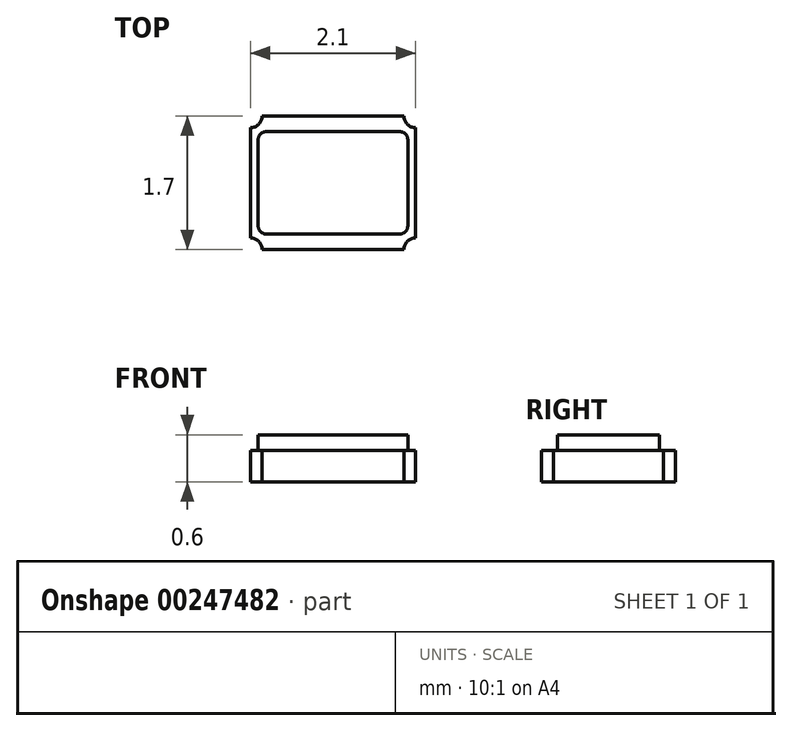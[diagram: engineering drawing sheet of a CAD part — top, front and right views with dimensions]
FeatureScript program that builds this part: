
annotation { "Feature Type Name" : "Feature", "Feature Type Description" : "" }
export const myFeature = defineFeature(function(context is Context, id is Id, definition is map)
    precondition{}
    {
        {
            var Q0;
            Q0=qCreatedBy(makeId("Top.planeOp"),FACE);
            var sketch = newSketch(context, id + "F0", { "sketchPlane" : qUnion([Q0])});
            skLineSegment(sketch, "E0.bottom", {"start": v(0.9, -0.85) * mm, "end": v(-0.9, -0.85) * mm});
            skLineSegment(sketch, "E0.top", {"start": v(0.9, 0.85) * mm, "end": v(-0.9, 0.85) * mm});
            skLineSegment(sketch, "E0.left", {"start": v(1.05, -0.7) * mm, "end": v(1.05, 0.7) * mm});
            skLineSegment(sketch, "E0.right", {"start": v(-1.05, -0.7) * mm, "end": v(-1.05, 0.7) * mm});
            skPoint(sketch, "E0.middle", {"position": v(0, 0) * mm});
            skArc(sketch, "E1", {"start": v(-0.9, 0.85) * mm, "mid": v(-0.94, 0.74) * mm, "end": v(-1.05, 0.7) * mm});
            skLineSegment(sketch, "E2", {"start": v(0, 0.85) * mm, "end": v(0, -0.85) * mm, "construction": true});
            skPoint(sketch, "E2.startSnap0", {"position": v(0.08, 0.85) * mm});
            skLineSegment(sketch, "E3", {"start": v(1.05, 0) * mm, "end": v(-1.05, 0) * mm, "construction": true});
            skLineSegment(sketch, "E4.MirrorCS", {"start": v(-0.9, 0.85) * mm, "end": v(0.9, 0.85) * mm});
            skArc(sketch, "E5.MirrorCS", {"start": v(0.9, 0.85) * mm, "mid": v(0.94, 0.74) * mm, "end": v(1.05, 0.7) * mm});
            skLineSegment(sketch, "E6.MirrorCS", {"start": v(-1.05, 0) * mm, "end": v(1.05, 0) * mm, "construction": true});
            skArc(sketch, "E7.MirrorCS", {"start": v(-0.9, -0.85) * mm, "mid": v(-0.94, -0.74) * mm, "end": v(-1.05, -0.7) * mm});
            skLineSegment(sketch, "E8.MirrorCS", {"start": v(-1.05, 0.7) * mm, "end": v(-1.05, -0.7) * mm});
            skLineSegment(sketch, "E9.MirrorCS", {"start": v(-0.9, -0.85) * mm, "end": v(0.9, -0.85) * mm});
            skArc(sketch, "E10.MirrorCS", {"start": v(0.9, -0.85) * mm, "mid": v(0.94, -0.74) * mm, "end": v(1.05, -0.7) * mm});
            skSolve(sketch);
        }
        {
            var Q0;
            Q0=qSketchRegion(id+"F0",true);
            extrude(context, id + "F1", {"entities" : qUnion([Q0]), "depth" : 0.6 * mm});
        }
        {
            var Q0;
            Q0=makeQuery(id+"F1.opExtrude","CAP_FACE",FACE,{"disambiguationData":[OSD([sQuery(id+"F0.wireOp",EDGE,"E4.MirrorCS"),sQuery(id+"F0.wireOp",EDGE,"E0.left"),sQuery(id+"F0.wireOp",EDGE,"E5.MirrorCS"),sQuery(id+"F0.wireOp",EDGE,"E1"),sQuery(id+"F0.wireOp",EDGE,"E7.MirrorCS"),sQuery(id+"F0.wireOp",EDGE,"E8.MirrorCS"),sQuery(id+"F0.wireOp",EDGE,"E9.MirrorCS"),sQuery(id+"F0.wireOp",EDGE,"E10.MirrorCS")])],"isStart":false});
            var sketch = newSketch(context, id + "F2", { "sketchPlane" : qUnion([Q0])});
            skLineSegment(sketch, "E11.bottom", {"start": v(0.85, -0.65) * mm, "end": v(-0.85, -0.65) * mm});
            skLineSegment(sketch, "E11.top", {"start": v(0.85, 0.65) * mm, "end": v(-0.85, 0.65) * mm});
            skLineSegment(sketch, "E11.left", {"start": v(0.95, -0.55) * mm, "end": v(0.95, 0.55) * mm});
            skLineSegment(sketch, "E11.right", {"start": v(-0.95, -0.55) * mm, "end": v(-0.95, 0.55) * mm});
            skPoint(sketch, "E11.middle", {"position": v(0, 0) * mm});
            skPoint(sketch, "E12.visualSharp", {"position": v(-0.95, 0.65) * mm});
            skArc(sketch, "E12.filletArc", {"start": v(-0.85, 0.65) * mm, "mid": v(-0.92, 0.62) * mm, "end": v(-0.95, 0.55) * mm});
            skPoint(sketch, "E13.visualSharp", {"position": v(0.95, 0.65) * mm});
            skArc(sketch, "E13.filletArc", {"start": v(0.95, 0.55) * mm, "mid": v(0.92, 0.62) * mm, "end": v(0.85, 0.65) * mm});
            skPoint(sketch, "E14.visualSharp", {"position": v(0.95, -0.65) * mm});
            skArc(sketch, "E14.filletArc", {"start": v(0.85, -0.65) * mm, "mid": v(0.92, -0.62) * mm, "end": v(0.95, -0.55) * mm});
            skPoint(sketch, "E15.visualSharp", {"position": v(-0.95, -0.65) * mm});
            skArc(sketch, "E15.filletArc", {"start": v(-0.95, -0.55) * mm, "mid": v(-0.92, -0.62) * mm, "end": v(-0.85, -0.65) * mm});
            skLineSegment(sketch, "E16.bottom", {"start": v(1.87, -1.48) * mm, "end": v(-1.87, -1.48) * mm});
            skLineSegment(sketch, "E16.top", {"start": v(1.87, 1.48) * mm, "end": v(-1.87, 1.48) * mm});
            skLineSegment(sketch, "E16.left", {"start": v(1.87, -1.48) * mm, "end": v(1.87, 1.48) * mm});
            skLineSegment(sketch, "E16.right", {"start": v(-1.87, -1.48) * mm, "end": v(-1.87, 1.48) * mm});
            skSolve(sketch);
        }
        {
            var Q0;
            Q0=qSketchRegion(id+"F2",true);
            extrude(context, id + "F3", {"entities" : qUnion([Q0]), "oppositeDirection" : true, "depth" : .2 * mm});
        }
        {
            var Q0;
            Q0=makeQuery(id+"F3.opExtrude","SWEPT_BODY",BODY,{"disambiguationData":[OSD([sQuery(id+"F2.wireOp",EDGE,"E11.bottom"),sQuery(id+"F2.wireOp",EDGE,"E11.top"),sQuery(id+"F2.wireOp",EDGE,"E11.left"),sQuery(id+"F2.wireOp",EDGE,"E11.right"),sQuery(id+"F2.wireOp",EDGE,"E12.filletArc"),sQuery(id+"F2.wireOp",EDGE,"E13.filletArc"),sQuery(id+"F2.wireOp",EDGE,"E14.filletArc"),sQuery(id+"F2.wireOp",EDGE,"E15.filletArc"),sQuery(id+"F2.wireOp",EDGE,"E16.bottom"),sQuery(id+"F2.wireOp",EDGE,"E16.top"),sQuery(id+"F2.wireOp",EDGE,"E16.left"),sQuery(id+"F2.wireOp",EDGE,"E16.right")])]});
            var Q1;
            Q1=makeQuery(id+"F1.opExtrude","SWEPT_BODY",BODY,{"disambiguationData":[OSD([sQuery(id+"F0.wireOp",EDGE,"E4.MirrorCS"),sQuery(id+"F0.wireOp",EDGE,"E0.left"),sQuery(id+"F0.wireOp",EDGE,"E5.MirrorCS"),sQuery(id+"F0.wireOp",EDGE,"E1"),sQuery(id+"F0.wireOp",EDGE,"E7.MirrorCS"),sQuery(id+"F0.wireOp",EDGE,"E8.MirrorCS"),sQuery(id+"F0.wireOp",EDGE,"E9.MirrorCS"),sQuery(id+"F0.wireOp",EDGE,"E10.MirrorCS")])]});
            booleanBodies(context, id + "F4", {"operationType" : BooleanOperationType.SUBTRACTION, "tools" : qUnion([Q0]), "targets" : qUnion([Q1])});
        }
    });
